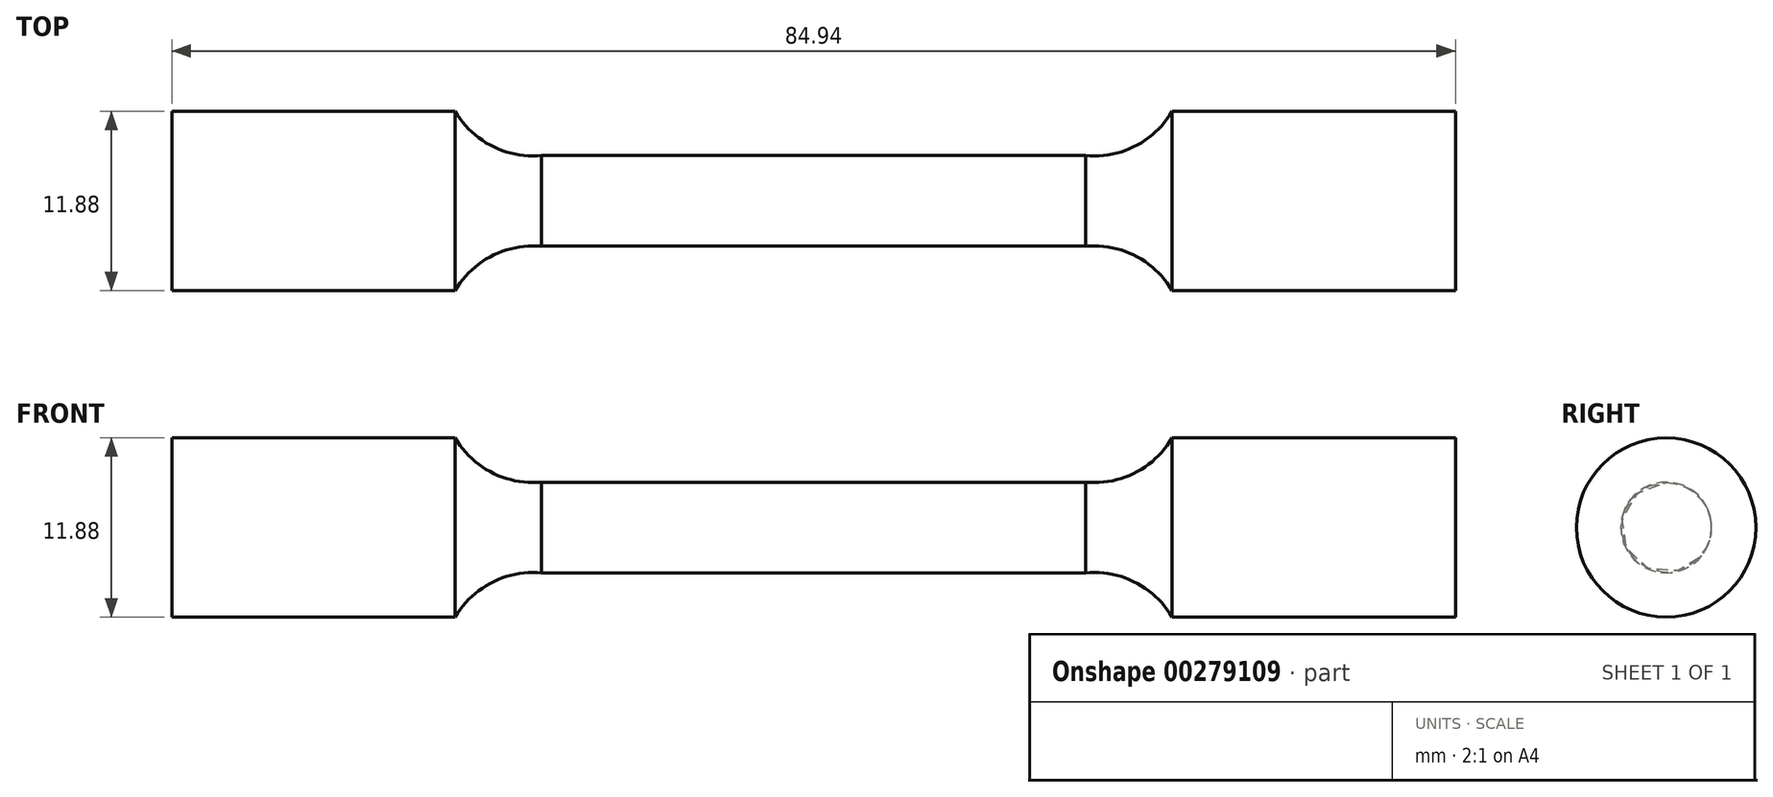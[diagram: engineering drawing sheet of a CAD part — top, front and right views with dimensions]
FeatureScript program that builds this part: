
annotation { "Feature Type Name" : "Feature", "Feature Type Description" : "" }
export const myFeature = defineFeature(function(context is Context, id is Id, definition is map)
    precondition{}
    {
        {
            var Q0;
            Q0=qCreatedBy(makeId("Front.planeOp"),FACE);
            var sketch = newSketch(context, id + "F0", { "sketchPlane" : qUnion([Q0])});
            skLineSegment(sketch, "E0", {"start": v(0, 3) * mm, "end": v(18, 3) * mm});
            skArc(sketch, "E1", {"start": v(18, 3) * mm, "mid": v(21.29, 3.64) * mm, "end": v(23.72, 5.94) * mm});
            skLineSegment(sketch, "E2", {"start": v(23.72, 5.94) * mm, "end": v(42.47, 5.94) * mm});
            skLineSegment(sketch, "E3", {"start": v(42.47, 5.94) * mm, "end": v(42.47, 0) * mm});
            skLineSegment(sketch, "E4.MirrorCS", {"start": v(0, 3) * mm, "end": v(-18, 3) * mm});
            skLineSegment(sketch, "E5.MirrorCS", {"start": v(-42.47, 5.94) * mm, "end": v(-42.47, 0) * mm});
            skLineSegment(sketch, "E6.MirrorCS", {"start": v(-23.72, 5.94) * mm, "end": v(-42.47, 5.94) * mm});
            skArc(sketch, "E7.MirrorCS", {"start": v(-18, 3) * mm, "mid": v(-21.29, 3.64) * mm, "end": v(-23.72, 5.94) * mm});
            skLineSegment(sketch, "E8", {"start": v(-42.47, 0) * mm, "end": v(42.47, 0) * mm});
            skSolve(sketch);
        }
        {
            var Q0;
            Q0 = qSketchRegion(id + "F0", true);
            var Q1;
            Q1=sQuery(id+"F0.wireOp",EDGE,"E8");
            revolve(context, id + "F1", {"entities" : qUnion([Q0]), "axis" : qUnion([Q1]), "revolveType" : RevolveType.FULL});
        }
    });
